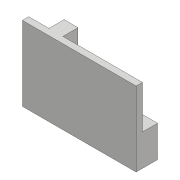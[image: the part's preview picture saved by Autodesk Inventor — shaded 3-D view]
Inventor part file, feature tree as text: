
AUTODESK INVENTOR PART (.ipt)
format: ipt  version: 2018 (Build 220112000, 112)  size: 91,648 bytes
history: native  units: mm
features: extrude x2, sketch x2
ambient origin geometry x8: Origin, YZ Plane, XZ Plane, XY Plane, X Axis, Y Axis, Z Axis, Center Point
bodies: Solid1 (feature_tree)
feature tree (4):
  extrude  "Extrusion1"  Depth=90.0mm
  extrude  "Extrusion2"  Depth=25.0mm
  sketch  "Sketch1"  dims[d0=59.0mm d1=90.0mm]
  sketch  "Sketch2"  dims[d2=17.0mm d3=0.0mm d4=25.0mm d5=25.0mm d6=16.0mm d7=63.0mm d8=12.0mm d9=0.0mm]
